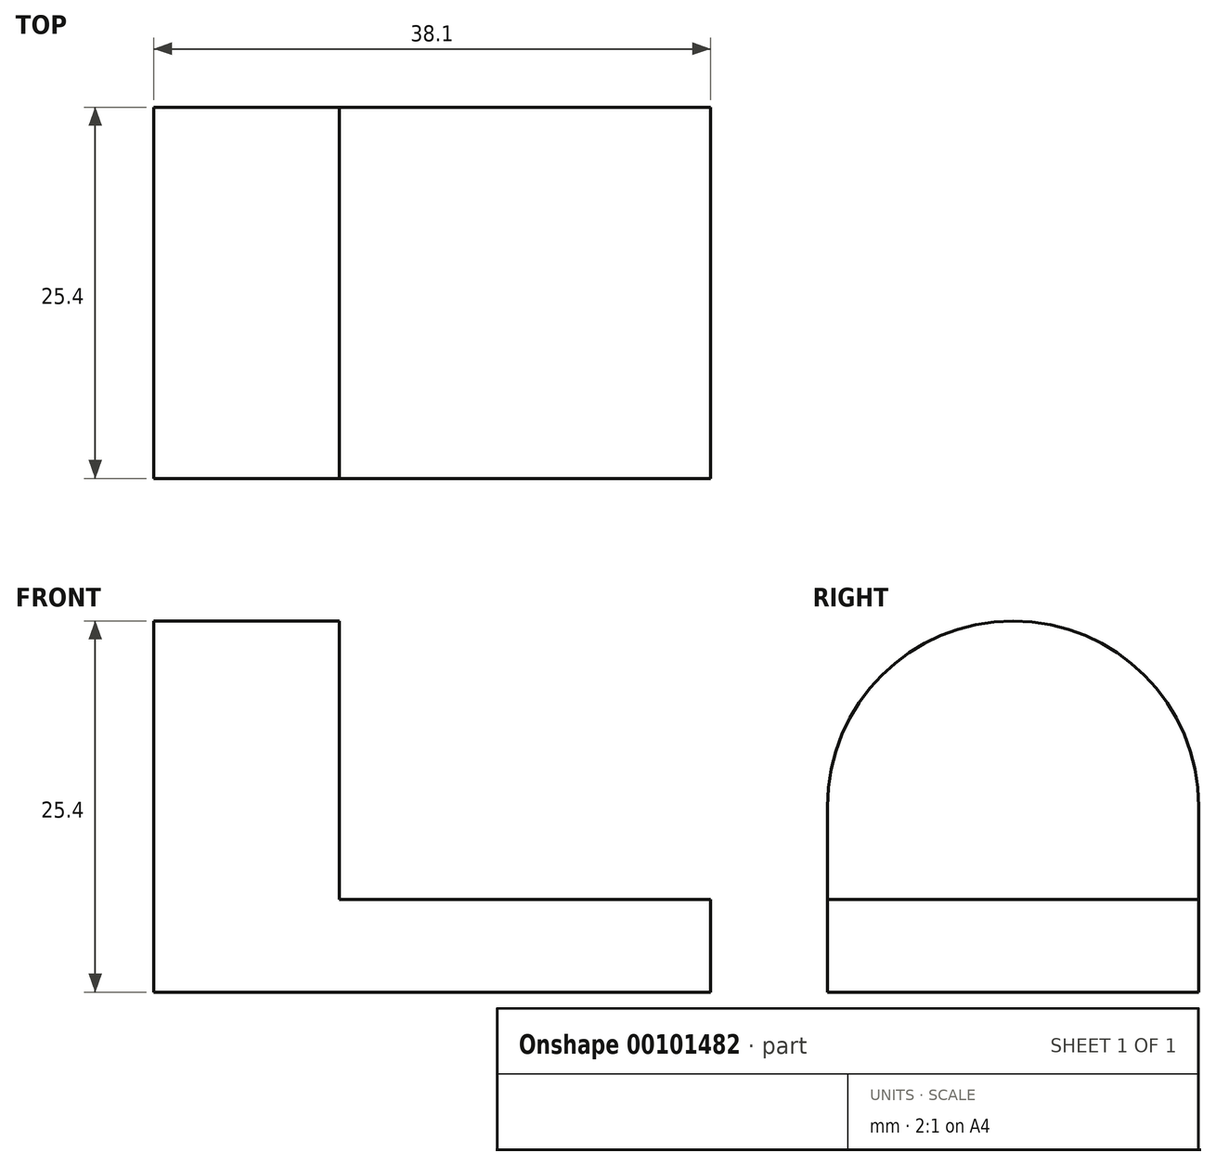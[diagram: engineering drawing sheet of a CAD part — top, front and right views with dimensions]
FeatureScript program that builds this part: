
annotation { "Feature Type Name" : "Feature", "Feature Type Description" : "" }
export const myFeature = defineFeature(function(context is Context, id is Id, definition is map)
    precondition{}
    {
        {
            var Q0;
            Q0=qCreatedBy(makeId("Right.planeOp"),FACE);
            var sketch = newSketch(context, id + "F0", { "sketchPlane" : qUnion([Q0])});
            skLineSegment(sketch, "E0", {"start": v(0, 0) * mm, "end": v(0, 12.7) * mm});
            skLineSegment(sketch, "E1", {"start": v(0, 0) * mm, "end": v(-25.4, 0) * mm});
            skLineSegment(sketch, "E2", {"start": v(-25.4, 0) * mm, "end": v(-25.4, 12.7) * mm});
            skArc(sketch, "E3", {"start": v(0, 12.7) * mm, "mid": v(-12.7, 25.4) * mm, "end": v(-25.4, 12.7) * mm});
            skSolve(sketch);
        }
        {
            var Q0;
            Q0=makeQuery(id+"F0.imprint","IMPRINT",FACE,{"disambiguationData":[TD([[makeQuery(id+"F0.imprint","IMPRINT",EDGE,{"derivedFrom":sQuery(id+"F0.wireOp",EDGE,"E0")}),1.0]])]});
            extrude(context, id + "F1", {"entities" : qUnion([Q0]), "depth" : 12.7 * mm});
        }
        {
            var Q0;
            Q0=qCreatedBy(makeId("Front.planeOp"),FACE);
            var sketch = newSketch(context, id + "F2", { "sketchPlane" : qUnion([Q0])});
            skLineSegment(sketch, "E4", {"start": v(0, 0) * mm, "end": v(38.1, 0) * mm});
            skLineSegment(sketch, "E5", {"start": v(38.1, 0) * mm, "end": v(38.1, 6.35) * mm});
            skLineSegment(sketch, "E6", {"start": v(38.1, 6.35) * mm, "end": v(0, 6.35) * mm});
            skLineSegment(sketch, "E7", {"start": v(0, 6.35) * mm, "end": v(0, 0) * mm});
            skSolve(sketch);
        }
        {
            var Q0;
            Q0=makeQuery(id+"F2.imprint","IMPRINT",FACE,{"disambiguationData":[TD([[makeQuery(id+"F2.imprint","IMPRINT",EDGE,{"derivedFrom":sQuery(id+"F2.wireOp",EDGE,"E4")}),1.0]])]});
            extrude(context, id + "F3", {"entities" : qUnion([Q0]), "operationType" : NewBodyOperationType.ADD, "depth" : 25.4 * mm});
        }
    });
